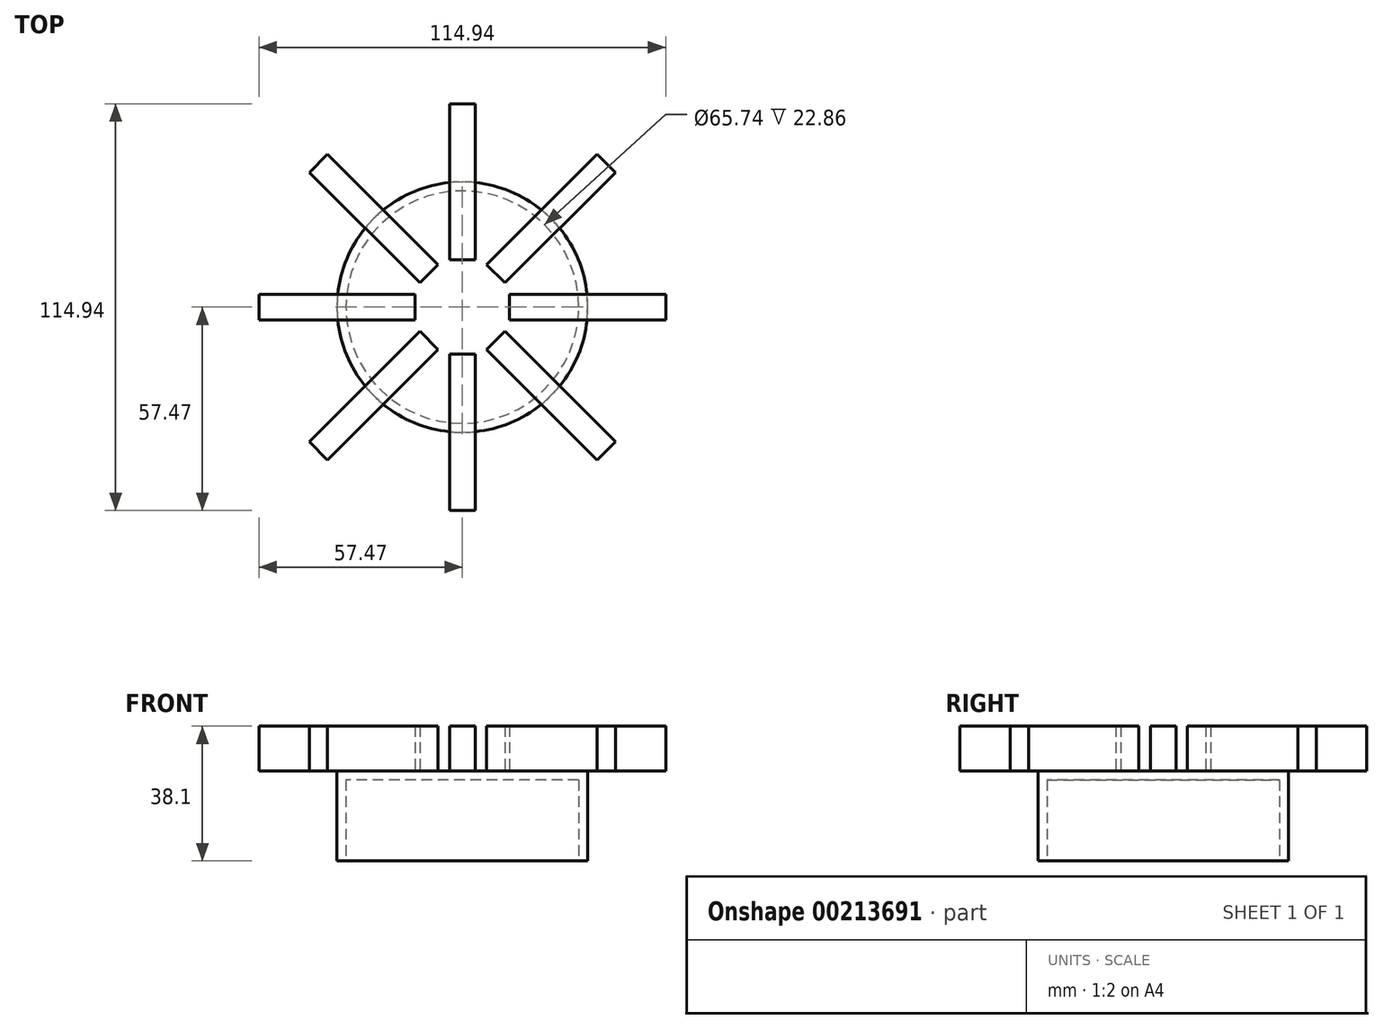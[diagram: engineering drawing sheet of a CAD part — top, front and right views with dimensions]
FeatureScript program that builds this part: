
annotation { "Feature Type Name" : "Feature", "Feature Type Description" : "" }
export const myFeature = defineFeature(function(context is Context, id is Id, definition is map)
    precondition{}
    {
        {
            var Q0;
            Q0=qCreatedBy(makeId("Top.planeOp"),FACE);
            var sketch = newSketch(context, id + "F0", { "sketchPlane" : qUnion([Q0])});
            skCircle(sketch, "E0", {"center": v(0, 0) * mm, "radius": 35.41 * mm});
            skSolve(sketch);
        }
        {
            var Q0;
            Q0 = qSketchRegion(id + "F0", true);
            extrude(context, id + "F1", {"entities" : qUnion([Q0]), "depth" : 25.4 * mm});
        }
        {
            var Q0;
            Q0=makeQuery(id+"F1.opExtrude","CAP_FACE",FACE,{"disambiguationData":[OSD([sQuery(id+"F0.wireOp",EDGE,"E0")])],"isStart":false});
            var sketch = newSketch(context, id + "F2", { "sketchPlane" : qUnion([Q0])});
            skLineSegment(sketch, "E1.bottom", {"start": v(57.47, 3.64) * mm, "end": v(13.35, 3.64) * mm});
            skLineSegment(sketch, "E1.top", {"start": v(57.47, -3.64) * mm, "end": v(13.35, -3.64) * mm});
            skLineSegment(sketch, "E1.left", {"start": v(57.47, 3.64) * mm, "end": v(57.47, -3.64) * mm});
            skLineSegment(sketch, "E1.right", {"start": v(13.35, 3.64) * mm, "end": v(13.35, -3.64) * mm});
            skPoint(sketch, "E1.middle", {"position": v(35.41, 0) * mm});
            skSolve(sketch);
        }
        {
            var Q0;
            Q0 = qSketchRegion(id + "F2", true);
            extrude(context, id + "F3", {"entities" : qUnion([Q0]), "depth" : 12.7 * mm});
        }
        {
            var Q0;
            Q0=makeQuery(id+"F3.opExtrude","SWEPT_BODY",BODY,{"disambiguationData":[OSD([sQuery(id+"F2.wireOp",EDGE,"E1.bottom"),sQuery(id+"F2.wireOp",EDGE,"E1.top"),sQuery(id+"F2.wireOp",EDGE,"E1.left"),sQuery(id+"F2.wireOp",EDGE,"E1.right")])]});
            var Q1;
            Q1=makeQuery(id+"F1.opExtrude","CAP_EDGE",EDGE,{"disambiguationData":[OSD([sQuery(id+"F0.wireOp",EDGE,"E0")])],"isStart":false});
            circularPattern(context, id + "F4", {"entities" : qUnion([Q0]), "axis" : qUnion([Q1]), "angle" : 360 * degree, "instanceCount" : 8, "equalSpace" : true});
        }
        {
            var Q0;
            Q0=makeQuery(id+"F1.opExtrude","CAP_FACE",FACE,{"disambiguationData":[OSD([sQuery(id+"F0.wireOp",EDGE,"E0")])],"isStart":true});
            shell(context, id + "F5", {"entities" : qUnion([Q0]), "thickness" : 2.54 * mm});
        }
    });
